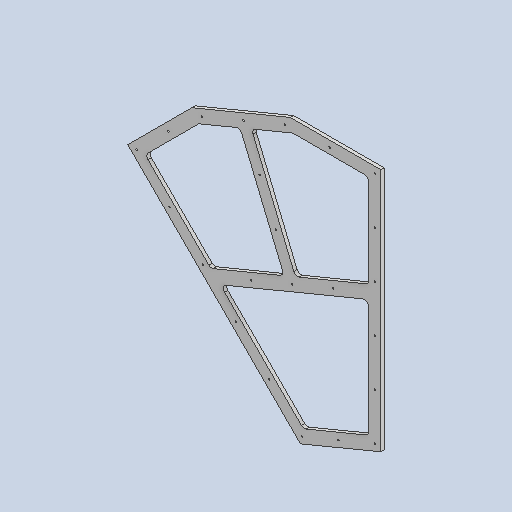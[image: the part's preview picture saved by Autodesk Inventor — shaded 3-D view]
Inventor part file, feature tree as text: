
AUTODESK INVENTOR PART (.ipt)
format: ipt  version: 2025 (Build 290162010, 162A)  size: 206,848 bytes
history: native  units: mm
features: sketch x4, extrude x3, fillet x1
ambient origin geometry x8: Origin, YZ Plane, XZ Plane, XY Plane, X Axis, Y Axis, Z Axis, Center Point
bodies: Solid1 (feature_tree)
feature tree (8):
  extrude  "Extrusion1"  Depth=260.0mm
  extrude  "Extrusion2"  Depth=8.0mm TaperAngle=0.0deg
  fillet  "Fillet1"  Radius=15.0mm
  extrude  "Extrusion4"  Depth=280.0mm
  sketch  "Sketch1"  dims[d0=513.0mm d2=260.0mm]
  sketch  "Sketch2"  dims[d11=30.0mm d12=280.0mm]
  sketch  "Sketch5"  dims[d13=30.0mm d14=30.0mm d15=15.0mm d16=0.0mm d17=0.0mm d18=10.0mm d21=30.0mm d22=30.0mm d23=30.0mm d24=30.0mm d32=15.0mm d33=15.0mm d34=15.0mm d35=4.0mm d37=103.33mm d38=103.33mm d41=60.0mm d43=114.2572mm d44=10.0mm d46=10.0mm d49=108.5mm d50=110.0mm d51=110.0mm d52=10.0mm d53=0.0mm]
  sketch  "Sketch Rectangular Pattern1"  dims[d3=635.0mm d5=8.0mm d6=0.0mm d10=15.0mm]
